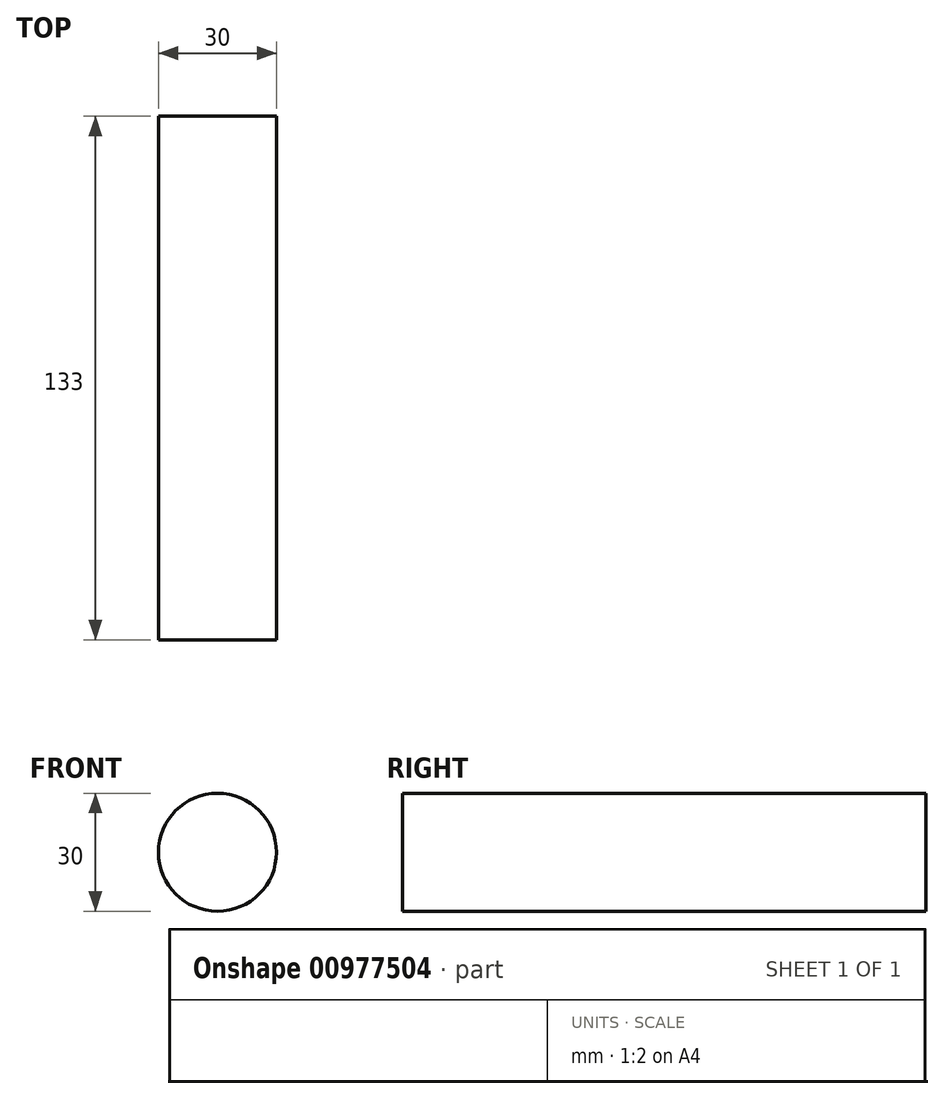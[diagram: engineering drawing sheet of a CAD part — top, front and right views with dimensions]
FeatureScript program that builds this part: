
annotation { "Feature Type Name" : "Feature", "Feature Type Description" : "" }
export const myFeature = defineFeature(function(context is Context, id is Id, definition is map)
    precondition{}
    {
        {
            var Q0;
            Q0=qCreatedBy(makeId("Front.planeOp"),FACE);
            var sketch = newSketch(context, id + "F0", { "sketchPlane" : qUnion([Q0])});
            skCircle(sketch, "E0", {"center": v(0, 0) * mm, "radius": 15 * mm});
            skSolve(sketch);
        }
        {
            var Q0;
            Q0 = qSketchRegion(id + "F0", true);
            extrude(context, id + "F1", {"entities" : qUnion([Q0]), "depth" : 133 * mm, "offsetDistance" : 25 * mm});
        }
    });
